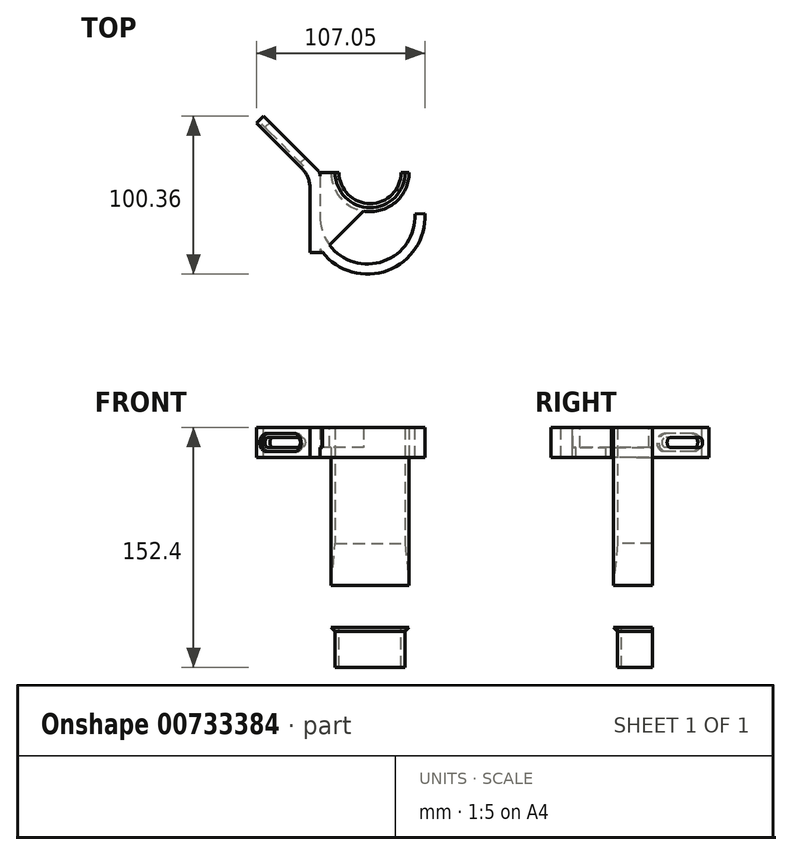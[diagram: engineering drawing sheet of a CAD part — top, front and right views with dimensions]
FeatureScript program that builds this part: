
annotation { "Feature Type Name" : "Feature", "Feature Type Description" : "" }
export const myFeature = defineFeature(function(context is Context, id is Id, definition is map)
    precondition{}
    {
        {
            var Q0;
            Q0=qCreatedBy(makeId("Top.planeOp"),FACE);
            var sketch = newSketch(context, id + "F0", { "sketchPlane" : qUnion([Q0])});
            skCircle(sketch, "E0", {"center": v(0, 0) * mm, "radius": 22.23 * mm});
            skCircle(sketch, "E1", {"center": v(0, 0) * mm, "radius": 24.77 * mm});
            skSolve(sketch);
        }
        {
            var Q0;
            Q0=makeQuery(id+"F0.imprint","IMPRINT",FACE,{"disambiguationData":[TD([[makeQuery(id+"F0.imprint","IMPRINT",EDGE,{"derivedFrom":sQuery(id+"F0.wireOp",EDGE,"E0")}),-1.0]])]});
            var sketch = newSketch(context, id + "F1", { "sketchPlane" : qUnion([Q0])});
            skSolve(sketch);
        }
        {
            var Q0;
            Q0=makeQuery(id+"F1.imprint","IMPRINT",FACE,{"disambiguationData":[TD([[makeQuery(id+"F1.imprint","IMPRINT",EDGE,{"derivedFrom":makeQuery(id+"F0.imprint","IMPRINT",EDGE,{"derivedFrom":sQuery(id+"F0.wireOp",EDGE,"E0")})}),-1.0]])]});
            extrude(context, id + "F2", {"entities" : qUnion([Q0]), "depth" : 127 * mm, "offsetDistance" : 25.4 * mm});
        }
        {
            var Q0;
            Q0=qCreatedBy(makeId("Top.planeOp"),FACE);
            var sketch = newSketch(context, id + "F3", { "sketchPlane" : qUnion([Q0])});
            skLineSegment(sketch, "E2.bottom", {"start": v(38.25, 0) * mm, "end": v(-119.23, 0) * mm});
            skLineSegment(sketch, "E2.top", {"start": v(38.25, 78.16) * mm, "end": v(-119.23, 78.16) * mm});
            skLineSegment(sketch, "E2.left", {"start": v(38.25, 0) * mm, "end": v(38.25, 78.16) * mm});
            skLineSegment(sketch, "E2.right", {"start": v(-119.23, 0) * mm, "end": v(-119.23, 78.16) * mm});
            skPoint(sketch, "E2.middle", {"position": v(-40.5, 39.08) * mm});
            skSolve(sketch);
        }
        {
            var Q0;
            Q0=makeQuery(id+"F3.imprint","IMPRINT",FACE,{"disambiguationData":[TD([[makeQuery(id+"F3.imprint","IMPRINT",EDGE,{"derivedFrom":sQuery(id+"F3.wireOp",EDGE,"E2.bottom")}),-1.0]])]});
            extrude(context, id + "F4", {"entities" : qUnion([Q0]), "operationType" : NewBodyOperationType.REMOVE, "endBound" : BoundingType.SYMMETRIC, "oppositeDirection" : true, "depth" : 508 * mm, "offsetDistance" : 25.4 * mm});
        }
        {
            var Q0;
            Q0=qCreatedBy(makeId("Top.planeOp"),FACE);
            cPlane(context, id + "F5", {"entities" : qUnion([Q0]), "cplaneType" : CPlaneType.OFFSET, "offset" : 50.8 * mm, "width" : 152.4 * mm, "height" : 152.4 * mm});
        }
        {
            var Q0;
            Q0=qCreatedBy(makeId("Top.planeOp"),FACE);
            var sketch = newSketch(context, id + "F6", { "sketchPlane" : qUnion([Q0])});
            skArc(sketch, "E3.0", {"start": v(-22.23, 0) * mm, "mid": v(0, -22.23) * mm, "end": v(22.23, 0) * mm});
            skArc(sketch, "E4.0", {"start": v(-19.69, 0) * mm, "mid": v(0, -19.69) * mm, "end": v(19.69, 0) * mm});
            skLineSegment(sketch, "E5", {"start": v(19.69, 0) * mm, "end": v(22.23, 0) * mm});
            skLineSegment(sketch, "E6", {"start": v(22.23, 0) * mm, "end": v(-19.69, 0) * mm});
            skLineSegment(sketch, "E7", {"start": v(-19.69, 0) * mm, "end": v(-22.23, 0) * mm});
            skSolve(sketch);
        }
        {
            var Q0;
            Q0=makeQuery(id+"F6.imprint","IMPRINT",FACE,{"disambiguationData":[TD([[makeQuery(id+"F6.imprint","IMPRINT",EDGE,{"derivedFrom":sQuery(id+"F6.wireOp",EDGE,"E3.0")}),1.0]])]});
            extrude(context, id + "F7", {"entities" : qUnion([Q0]), "oppositeDirection" : true, "depth" : 25.4 * mm, "offsetDistance" : 25.4 * mm});
        }
        {
            var Q0;
            Q0=qCreatedBy(makeId("Front.planeOp"),FACE);
            var sketch = newSketch(context, id + "F8", { "sketchPlane" : qUnion([Q0])});
            skLineSegment(sketch, "E8.0", {"start": v(22.23, 0) * mm, "end": v(24.77, 0) * mm});
            skLineSegment(sketch, "E9.0", {"start": v(22.23, -2.54) * mm, "end": v(22.23, 0) * mm});
            skPoint(sketch, "E10.orphan", {"position": v(-24.77, 0) * mm});
            skLineSegment(sketch, "E11", {"start": v(24.77, 0) * mm, "end": v(22.23, -2.54) * mm});
            skPoint(sketch, "E12.orphan", {"position": v(22.23, -25.4) * mm});
            skSolve(sketch);
        }
        {
            var Q0;
            Q0=makeQuery(id+"F8.imprint","IMPRINT",FACE,{"disambiguationData":[TD([[makeQuery(id+"F8.imprint","IMPRINT",EDGE,{"derivedFrom":sQuery(id+"F8.wireOp",EDGE,"E8.0")}),-1.0]])]});
            var Q1;
            Q1=makeQuery(id+"F7.opExtrude","SWEPT_FACE",FACE,{"disambiguationData":[OSD([sQuery(id+"F6.wireOp",EDGE,"E4.0")])]});
            revolve(context, id + "F9", {"surfaceOperationType" : NewSurfaceOperationType.NEW, "entities" : qUnion([Q0]), "axis" : qUnion([Q1]), "revolveType" : RevolveType.ONE_DIRECTION, "angle" : 180 * degree});
        }
        {
            var Q0;
            Q0=makeQuery(id+"F2.opExtrude","CAP_EDGE",EDGE,{"disambiguationData":[OSD([sQuery(id+"F0.wireOp",EDGE,"E0")])],"isStart":true});
            chamfer(context, id + "F10", {"entities" : qUnion([Q0]), "chamferType" : ChamferType.TWO_OFFSETS, "width1" : 5.08 * mm, "oppositeDirection" : false, "width2" : 53.34 * mm, "tangentPropagation" : true});
        }
        {
            var Q0;
            Q0=qCreatedBy(makeId("Right.planeOp"),FACE);
            cPlane(context, id + "F11", {"entities" : qUnion([Q0]), "cplaneType" : CPlaneType.OFFSET, "offset" : 31.75 * mm, "oppositeDirection" : true, "width" : 152.4 * mm, "height" : 152.4 * mm});
        }
        {
            var Q0;
            Q0=qCreatedBy(id+"F11.planeOp",FACE);
            var sketch = newSketch(context, id + "F12", { "sketchPlane" : qUnion([Q0])});
            skLineSegment(sketch, "E13.bottom", {"start": v(0, 127) * mm, "end": v(-50.8, 127) * mm});
            skLineSegment(sketch, "E13.top", {"start": v(0, 114.3) * mm, "end": v(-50.8, 114.3) * mm});
            skLineSegment(sketch, "E13.left", {"start": v(0, 127) * mm, "end": v(0, 114.3) * mm});
            skLineSegment(sketch, "E13.right", {"start": v(-50.8, 127) * mm, "end": v(-50.8, 114.3) * mm});
            skSolve(sketch);
        }
        {
            var Q0;
            Q0=makeQuery(id+"F12.imprint","IMPRINT",FACE,{"disambiguationData":[TD([[makeQuery(id+"F12.imprint","IMPRINT",EDGE,{"derivedFrom":sQuery(id+"F12.wireOp",EDGE,"E13.bottom")}),1.0]])]});
            var Q1;
            Q1=makeQuery(id+"F2.opExtrude","SWEPT_FACE",FACE,{"disambiguationData":[OSD([sQuery(id+"F0.wireOp",EDGE,"E1")])]});
            var Q2;
            Q2=makeQuery(id+"F2.opExtrude","SWEPT_BODY",BODY,{"disambiguationData":[OSD([sQuery(id+"F0.wireOp",EDGE,"E0"),sQuery(id+"F0.wireOp",EDGE,"E1")])]});
            extrude(context, id + "F13", {"entities" : qUnion([Q0]), "operationType" : NewBodyOperationType.ADD, "depth" : 31.75 * mm, "endBoundEntityFace" : qUnion([Q1]), "endBoundEntityBody" : qUnion([Q2]), "offsetDistance" : 25.4 * mm});
        }
        {
            var Q0;
            Q0=makeQuery(id+"F13.boolean.opBoolean","MERGE",FACE,{"derivedFrom":[makeQuery(id+"F2.opExtrude","CAP_FACE",FACE,{"disambiguationData":[OSD([sQuery(id+"F0.wireOp",EDGE,"E0"),sQuery(id+"F0.wireOp",EDGE,"E1")])],"isStart":false}),makeQuery(id+"F13.opExtrude","SWEPT_FACE",FACE,{"disambiguationData":[OSD([sQuery(id+"F12.wireOp",EDGE,"E13.bottom")])]})]});
            var sketch = newSketch(context, id + "F14", { "sketchPlane" : qUnion([Q0])});
            skCircle(sketch, "E14", {"center": v(0, 0) * mm, "radius": 22.23 * mm});
            skSolve(sketch);
        }
        {
            var Q0;
            {var subQ0=sQuery(id+"F14.wireOp",EDGE,"E14");var subQ1=makeQuery(id+"F4.opExtrude","SWEPT_FACE",FACE,{"disambiguationData":[OSD([sQuery(id+"F3.wireOp",EDGE,"E2.bottom")])]});var subQ2=sQuery(id+"F0.wireOp",EDGE,"E0");var subQ3=makeQuery(id+"F2.opExtrude","CAP_FACE",FACE,{"disambiguationData":[OSD([subQ2,sQuery(id+"F0.wireOp",EDGE,"E1")])],"isStart":false});var subQ4=makeQuery(id+"F14.imprint","INTERSECT",VERTEX,{"derivedFrom":[makeQuery(id+"F4.boolean.opBoolean","INTERSECT",EDGE,{"disambiguationData":[OD(1.0)],"derivedFrom":[subQ3,subQ1]}),subQ0]});Q0=makeQuery(id+"F14.imprint","IMPRINT",FACE,{"disambiguationData":[TD([[makeQuery(id+"F14.imprint","IMPRINT",EDGE,{"disambiguationData":[TD([[subQ4,-1.0]])],"derivedFrom":subQ0}),1.0]])]});}
            var Q1;
            {var subQ2=sQuery(id+"F0.wireOp",EDGE,"E0");var subQ4=sQuery(id+"F12.wireOp",EDGE,"E13.bottom");var subQ6=makeQuery(id+"F13.boolean.opBoolean","SPLIT",EDGE,{"disambiguationData":[TD([makeQuery(id+"F2.opExtrude","SWEPT_FACE",FACE,{"disambiguationData":[OSD([subQ2])]})])],"derivedFrom":makeQuery(id+"F13.opExtrude","CAP_EDGE",EDGE,{"disambiguationData":[OSD([subQ4])],"isStart":false})});Q1=makeQuery(id+"F14.imprint","IMPRINT",FACE,{"disambiguationData":[TD([[makeQuery(id+"F14.imprint","IMPRINT",EDGE,{"derivedFrom":subQ6}),-1.0]])]});}
            extrude(context, id + "F15", {"entities" : qUnion([Q0, Q1]), "operationType" : NewBodyOperationType.REMOVE, "oppositeDirection" : true, "depth" : 15.24 * mm, "offsetDistance" : 25.4 * mm});
        }
        {
            var Q0;
            Q0=makeQuery(id+"F13.opExtrude","CAP_EDGE",EDGE,{"disambiguationData":[OSD([sQuery(id+"F12.wireOp",EDGE,"E13.right")])],"isStart":false});
            chamfer(context, id + "F16", {"entities" : qUnion([Q0]), "width" : 30.48 * mm, "tangentPropagation" : true});
        }
        {
            var Q0;
            Q0=makeQuery(id+"F13.boolean.opBoolean","MERGE",FACE,{"derivedFrom":[makeQuery(id+"F2.opExtrude","CAP_FACE",FACE,{"disambiguationData":[OSD([sQuery(id+"F0.wireOp",EDGE,"E0"),sQuery(id+"F0.wireOp",EDGE,"E1")])],"isStart":false}),makeQuery(id+"F13.opExtrude","SWEPT_FACE",FACE,{"disambiguationData":[OSD([sQuery(id+"F12.wireOp",EDGE,"E13.bottom")])]})]});
            var sketch = newSketch(context, id + "F17", { "sketchPlane" : qUnion([Q0])});
            skLineSegment(sketch, "E15.0", {"start": v(-31.75, 0) * mm, "end": v(-31.75, -50.8) * mm});
            skLineSegment(sketch, "E16", {"start": v(-31.75, 0) * mm, "end": v(-67.67, 35.92) * mm});
            skLineSegment(sketch, "E17.0", {"start": v(-38.1, -2.63) * mm, "end": v(-72.16, 31.43) * mm});
            skLineSegment(sketch, "E18.0", {"start": v(-38.1, -2.63) * mm, "end": v(-38.1, -50.8) * mm});
            skLineSegment(sketch, "E19", {"start": v(-31.75, -50.8) * mm, "end": v(-38.1, -50.8) * mm});
            skLineSegment(sketch, "E20", {"start": v(-67.67, 35.92) * mm, "end": v(-72.16, 31.43) * mm});
            skSolve(sketch);
        }
        {
            var Q0;
            Q0=makeQuery(id+"F17.imprint","IMPRINT",FACE,{"disambiguationData":[TD([[makeQuery(id+"F17.imprint","IMPRINT",EDGE,{"derivedFrom":sQuery(id+"F17.wireOp",EDGE,"E15.0")}),-1.0]])]});
            extrude(context, id + "F18", {"entities" : qUnion([Q0]), "oppositeDirection" : true, "depth" : 19.05 * mm, "offsetDistance" : 25.4 * mm});
        }
        {
            var Q0;
            Q0=makeQuery(id+"F18.opExtrude","SWEPT_FACE",FACE,{"disambiguationData":[OSD([sQuery(id+"F17.wireOp",EDGE,"E17.0")])]});
            var sketch = newSketch(context, id + "F19", { "sketchPlane" : qUnion([Q0])});
            skLineSegment(sketch, "E21.bottom", {"start": v(-64.36, 111.68) * mm, "end": v(-38.96, 111.68) * mm});
            skLineSegment(sketch, "E21.top", {"start": v(-64.36, 123.24) * mm, "end": v(-38.96, 123.24) * mm});
            skArc(sketch, "E22", {"start": v(-38.96, 111.68) * mm, "mid": v(-33.18, 117.46) * mm, "end": v(-38.96, 123.24) * mm});
            skArc(sketch, "E23", {"start": v(-64.36, 123.24) * mm, "mid": v(-70.14, 117.46) * mm, "end": v(-64.36, 111.68) * mm});
            skLineSegment(sketch, "E24.0", {"start": v(-64.36, 114.22) * mm, "end": v(-38.96, 114.22) * mm});
            skArc(sketch, "E24.1", {"start": v(-64.36, 120.7) * mm, "mid": v(-67.6, 117.46) * mm, "end": v(-64.36, 114.22) * mm});
            skLineSegment(sketch, "E24.2", {"start": v(-64.36, 120.7) * mm, "end": v(-38.96, 120.7) * mm});
            skArc(sketch, "E24.3", {"start": v(-38.96, 114.22) * mm, "mid": v(-35.72, 117.46) * mm, "end": v(-38.96, 120.7) * mm});
            skSolve(sketch);
        }
        {
            var Q0;
            Q0=makeQuery(id+"F19.imprint","IMPRINT",FACE,{"disambiguationData":[TD([[makeQuery(id+"F19.imprint","IMPRINT",EDGE,{"derivedFrom":sQuery(id+"F19.wireOp",EDGE,"E24.0")}),1.0]])]});
            extrude(context, id + "F20", {"entities" : qUnion([Q0]), "operationType" : NewBodyOperationType.REMOVE, "oppositeDirection" : true, "depth" : 25.4 * mm, "offsetDistance" : 25.4 * mm});
        }
        {
            var Q0;
            Q0=makeQuery(id+"F19.imprint","IMPRINT",FACE,{"disambiguationData":[TD([[makeQuery(id+"F19.imprint","IMPRINT",EDGE,{"derivedFrom":sQuery(id+"F19.wireOp",EDGE,"E21.bottom")}),1.0]])]});
            extrude(context, id + "F21", {"entities" : qUnion([Q0]), "operationType" : NewBodyOperationType.REMOVE, "oppositeDirection" : true, "depth" : 1.9 * mm, "offsetDistance" : 25.4 * mm});
        }
        {
            var Q0;
            Q0=makeQuery(id+"F18.opExtrude","SWEPT_EDGE",EDGE,{"disambiguationData":[OSD([sQuery(id+"F17.wireOp",EDGE,"E17.0"),sQuery(id+"F17.wireOp",EDGE,"E18.0")])]});
            fillet(context, id + "F22", {"entities" : qUnion([Q0]), "radius" : 17.78 * mm, "tangentPropagation" : true, "allowEdgeOverflow" : false});
        }
        {
            var Q0;
            Q0=makeQuery(id+"F18.opExtrude","SWEPT_EDGE",EDGE,{"disambiguationData":[OSD([sQuery(id+"F0.wireOp",EDGE,"E0"),sQuery(id+"F0.wireOp",EDGE,"E1"),sQuery(id+"F3.wireOp",EDGE,"E2.bottom"),sQuery(id+"F12.wireOp",EDGE,"E13.bottom"),sQuery(id+"F12.wireOp",EDGE,"E13.left"),sQuery(id+"F17.wireOp",EDGE,"E15.0"),sQuery(id+"F17.wireOp",EDGE,"E16")])]});
            fillet(context, id + "F23", {"entities" : qUnion([Q0]), "radius" : 5.08 * mm, "tangentPropagation" : true, "allowEdgeOverflow" : false});
        }
        {
            var Q0;
            Q0=makeQuery(id+"F18.opExtrude","CAP_FACE",FACE,{"disambiguationData":[OSD([sQuery(id+"F17.wireOp",EDGE,"E15.0"),sQuery(id+"F17.wireOp",EDGE,"E17.0"),sQuery(id+"F17.wireOp",EDGE,"E18.0"),sQuery(id+"F17.wireOp",EDGE,"E16"),sQuery(id+"F17.wireOp",EDGE,"E19"),sQuery(id+"F17.wireOp",EDGE,"E20")])],"isStart":true});
            var sketch = newSketch(context, id + "F24", { "sketchPlane" : qUnion([Q0])});
            skArc(sketch, "E25", {"start": v(-31.75, -26.45) * mm, "mid": v(-1.62, -58.1) * mm, "end": v(28.5, -26.45) * mm});
            skPoint(sketch, "E25.endSnap0", {"position": v(-31.75, -26.45) * mm});
            skArc(sketch, "E26.0", {"start": v(-38.1, -26.14) * mm, "mid": v(-1.62, -64.44) * mm, "end": v(34.85, -26.14) * mm});
            skLineSegment(sketch, "E27", {"start": v(34.85, -26.14) * mm, "end": v(28.5, -26.45) * mm});
            skLineSegment(sketch, "E28", {"start": v(-31.75, -26.45) * mm, "end": v(-38.1, -26.14) * mm});
            skSolve(sketch);
        }
        {
            var Q0;
            {var subQ0=sQuery(id+"F24.wireOp",EDGE,"E27");Q0=makeQuery(id+"F24.imprint","IMPRINT",FACE,{"disambiguationData":[TD([[makeQuery(id+"F24.imprint","IMPRINT",EDGE,{"derivedFrom":subQ0}),1.0]])]});}
            var Q1;
            Q1=makeQuery(id+"F18.opExtrude","CAP_FACE",FACE,{"disambiguationData":[OSD([sQuery(id+"F17.wireOp",EDGE,"E15.0"),sQuery(id+"F17.wireOp",EDGE,"E17.0"),sQuery(id+"F17.wireOp",EDGE,"E18.0"),sQuery(id+"F17.wireOp",EDGE,"E16"),sQuery(id+"F17.wireOp",EDGE,"E19"),sQuery(id+"F17.wireOp",EDGE,"E20")])],"isStart":false});
            extrude(context, id + "F25", {"entities" : qUnion([Q0]), "operationType" : NewBodyOperationType.ADD, "endBound" : BoundingType.UP_TO_SURFACE, "oppositeDirection" : true, "depth" : 25.4 * mm, "endBoundEntityFace" : qUnion([Q1]), "offsetDistance" : 25.4 * mm});
        }
    });
